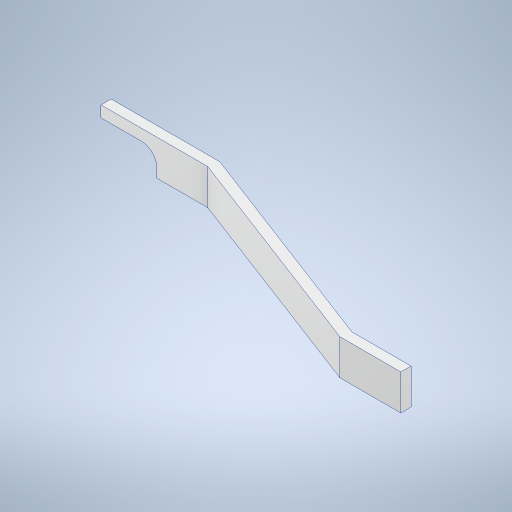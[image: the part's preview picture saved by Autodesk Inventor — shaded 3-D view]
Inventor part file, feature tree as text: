
AUTODESK INVENTOR PART (.ipt)
format: ipt  version: 2024 (Build 280153000, 153)  size: 257,536 bytes
history: native  units: mm
features: extrude x2, sketch x2, fillet x1
ambient origin geometry x8: Origin, YZ Plane, XZ Plane, XY Plane, X Axis, Y Axis, Z Axis, Center Point
bodies: Solid1 (feature_tree)
feature tree (5):
  extrude  "Extrusion1"  Depth=449.444101mm
  extrude  "Extrusion2"  Depth=30.0mm
  fillet  "Fillet1"  Radius=27.776137mm
  sketch  "Sketch1"  dims[d2=100.0mm d3=449.444101mm]
  sketch  "Sketch2"  dims[d4=120.0mm d5=27.776137mm d6=27.776137mm d7=20.0mm d8=70.0mm d9=0.0mm d10=110.0mm d11=0.0mm d12=30.0mm]
